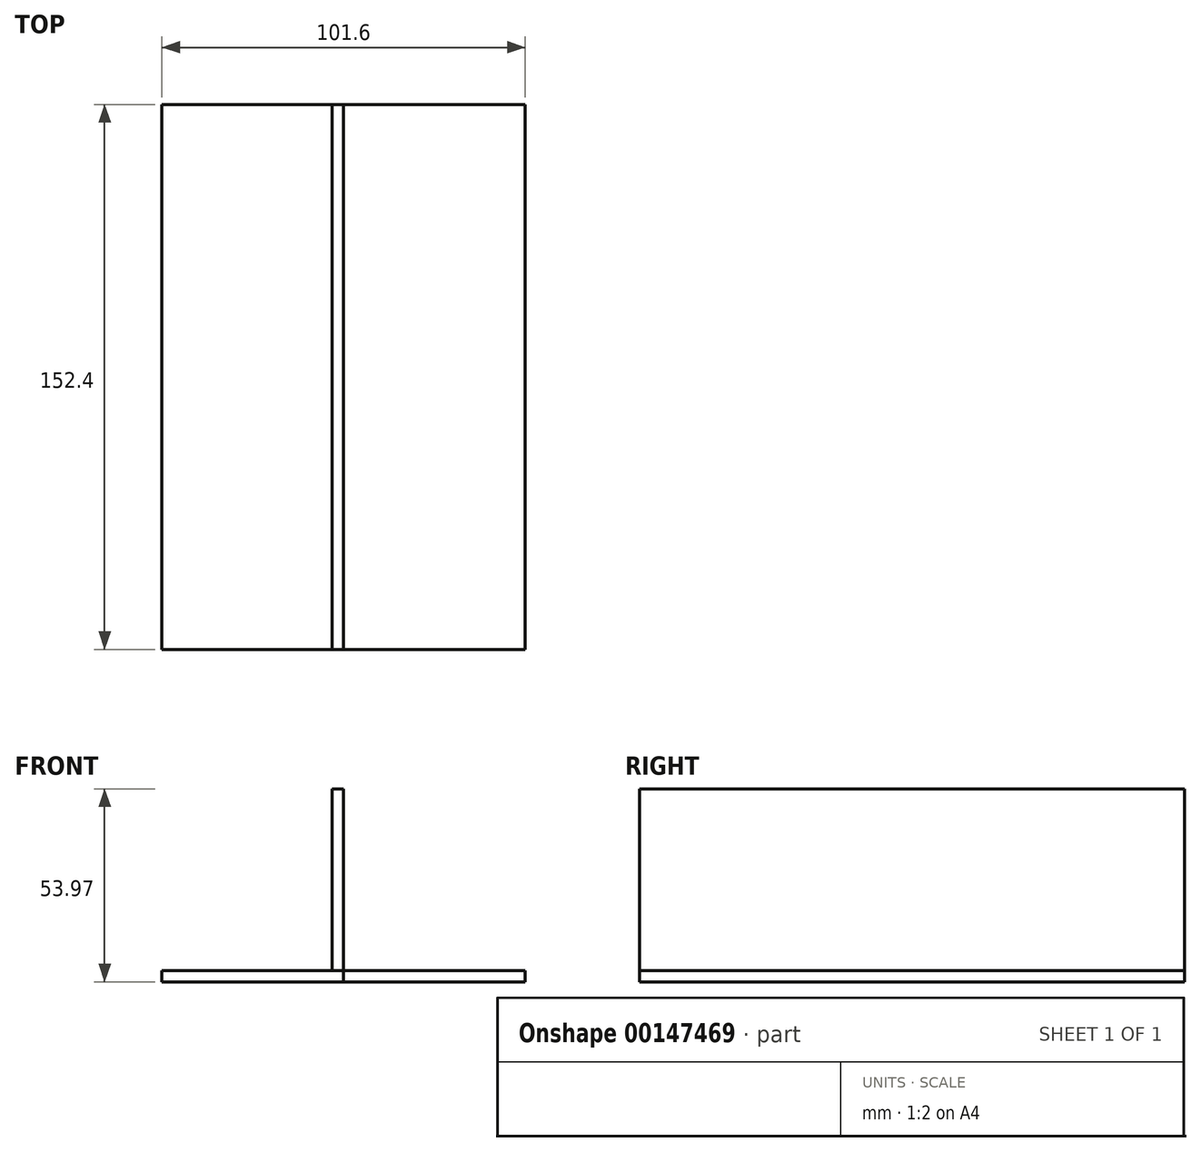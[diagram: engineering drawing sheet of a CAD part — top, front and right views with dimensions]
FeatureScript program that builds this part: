
annotation { "Feature Type Name" : "Feature", "Feature Type Description" : "" }
export const myFeature = defineFeature(function(context is Context, id is Id, definition is map)
    precondition{}
    {
        {
            var Q0;
            Q0=qCreatedBy(makeId("Front.planeOp"),FACE);
            var sketch = newSketch(context, id + "F0", { "sketchPlane" : qUnion([Q0])});
            skLineSegment(sketch, "E0.bottom", {"start": v(0, 0) * mm, "end": v(-3.18, 0) * mm});
            skLineSegment(sketch, "E0.top", {"start": v(0, 50.8) * mm, "end": v(-3.18, 50.8) * mm});
            skLineSegment(sketch, "E0.left", {"start": v(0, 0) * mm, "end": v(0, 50.8) * mm});
            skLineSegment(sketch, "E0.right", {"start": v(-3.18, 0) * mm, "end": v(-3.18, 50.8) * mm});
            skSolve(sketch);
        }
        {
            var Q0;
            Q0=makeQuery(id+"F0.imprint","IMPRINT",FACE,{"disambiguationData":[TD([[makeQuery(id+"F0.imprint","IMPRINT",EDGE,{"derivedFrom":sQuery(id+"F0.wireOp",EDGE,"E0.bottom")}),-1.0]])]});
            extrude(context, id + "F1", {"entities" : qUnion([Q0]), "endBound" : BoundingType.SYMMETRIC, "depth" : 152.4 * mm});
        }
        {
            var Q0;
            Q0=qCreatedBy(makeId("Front.planeOp"),FACE);
            var sketch = newSketch(context, id + "F2", { "sketchPlane" : qUnion([Q0])});
            skLineSegment(sketch, "E1.bottom", {"start": v(0, 0) * mm, "end": v(-50.8, 0) * mm});
            skLineSegment(sketch, "E1.top", {"start": v(0, -3.17) * mm, "end": v(-50.8, -3.17) * mm});
            skLineSegment(sketch, "E1.left", {"start": v(0, 0) * mm, "end": v(0, -3.17) * mm});
            skLineSegment(sketch, "E1.right", {"start": v(-50.8, 0) * mm, "end": v(-50.8, -3.17) * mm});
            skSolve(sketch);
        }
        {
            var Q0;
            Q0=makeQuery(id+"F2.imprint","IMPRINT",FACE,{"disambiguationData":[TD([[makeQuery(id+"F2.imprint","IMPRINT",EDGE,{"derivedFrom":sQuery(id+"F2.wireOp",EDGE,"E1.bottom")}),1.0]])]});
            extrude(context, id + "F3", {"entities" : qUnion([Q0]), "endBound" : BoundingType.SYMMETRIC, "depth" : 152.4 * mm});
        }
        {
            var Q0;
            Q0=qCreatedBy(makeId("Front.planeOp"),FACE);
            var sketch = newSketch(context, id + "F4", { "sketchPlane" : qUnion([Q0])});
            skLineSegment(sketch, "E2.bottom", {"start": v(0, 0) * mm, "end": v(50.8, 0) * mm});
            skLineSegment(sketch, "E2.top", {"start": v(0, -3.18) * mm, "end": v(50.8, -3.18) * mm});
            skLineSegment(sketch, "E2.left", {"start": v(0, 0) * mm, "end": v(0, -3.18) * mm});
            skLineSegment(sketch, "E2.right", {"start": v(50.8, 0) * mm, "end": v(50.8, -3.18) * mm});
            skSolve(sketch);
        }
        {
            var Q0;
            Q0=makeQuery(id+"F4.imprint","IMPRINT",FACE,{"disambiguationData":[TD([[makeQuery(id+"F4.imprint","IMPRINT",EDGE,{"derivedFrom":sQuery(id+"F4.wireOp",EDGE,"E2.bottom")}),-1.0]])]});
            extrude(context, id + "F5", {"entities" : qUnion([Q0]), "endBound" : BoundingType.SYMMETRIC, "depth" : 152.4 * mm});
        }
    });
